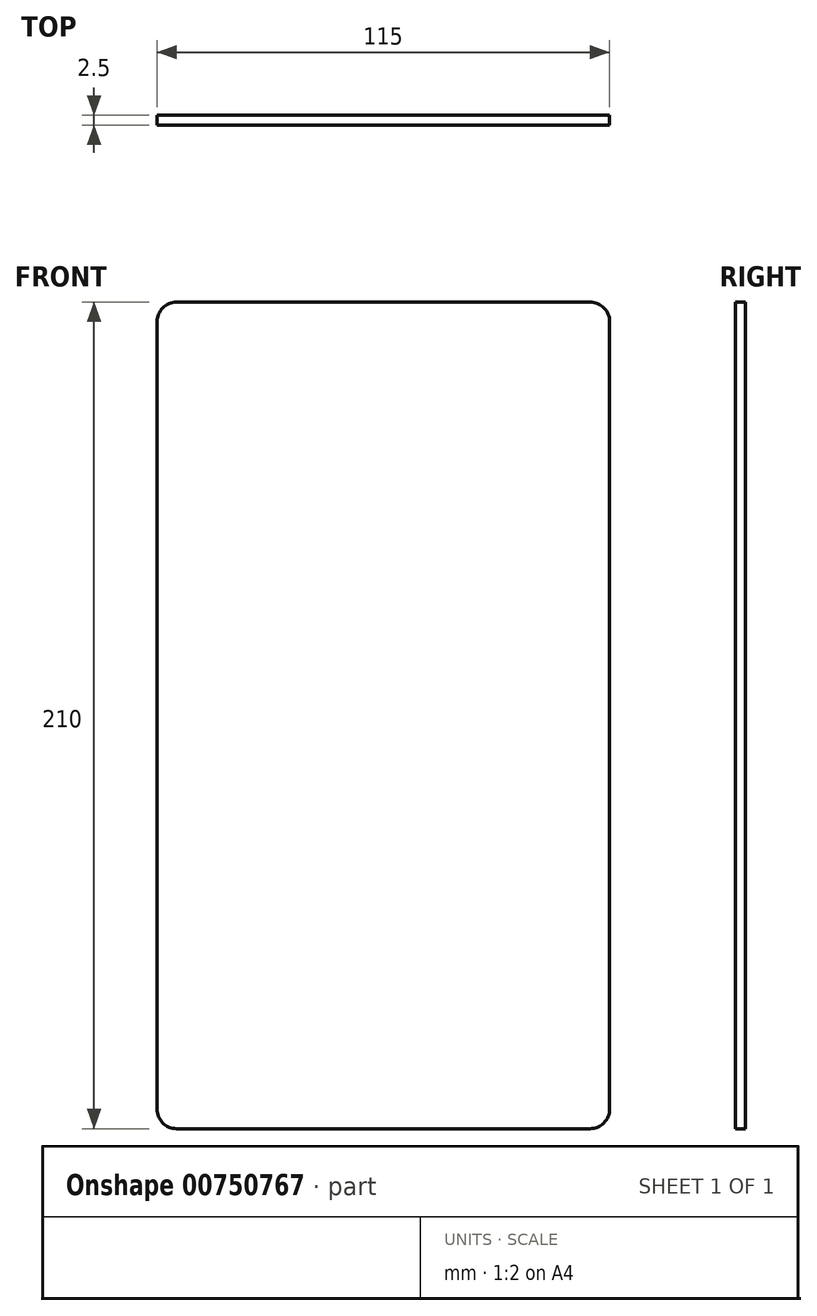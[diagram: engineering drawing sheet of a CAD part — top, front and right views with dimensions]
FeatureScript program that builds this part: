
annotation { "Feature Type Name" : "Feature", "Feature Type Description" : "" }
export const myFeature = defineFeature(function(context is Context, id is Id, definition is map)
    precondition{}
    {
        {
            var Q0;
            Q0=qCreatedBy(makeId("Front.planeOp"),FACE);
            var sketch = newSketch(context, id + "F0", { "sketchPlane" : qUnion([Q0])});
            skLineSegment(sketch, "E0.bottom", {"start": v(5, 0) * mm, "end": v(110, 0) * mm});
            skLineSegment(sketch, "E0.top", {"start": v(5, 210) * mm, "end": v(110, 210) * mm});
            skLineSegment(sketch, "E0.left", {"start": v(0, 5) * mm, "end": v(0, 205) * mm});
            skLineSegment(sketch, "E0.right", {"start": v(115, 5) * mm, "end": v(115, 205) * mm});
            skPoint(sketch, "E1.visualSharp", {"position": v(0, 210) * mm});
            skArc(sketch, "E1.filletArc", {"start": v(5, 210) * mm, "mid": v(1.46, 208.54) * mm, "end": v(0, 205) * mm});
            skPoint(sketch, "E2.visualSharp", {"position": v(115, 210) * mm});
            skArc(sketch, "E2.filletArc", {"start": v(115, 205) * mm, "mid": v(113.54, 208.54) * mm, "end": v(110, 210) * mm});
            skPoint(sketch, "E3.visualSharp", {"position": v(115, 0) * mm});
            skArc(sketch, "E3.filletArc", {"start": v(110, 0) * mm, "mid": v(113.54, 1.46) * mm, "end": v(115, 5) * mm});
            skPoint(sketch, "E4.visualSharp", {"position": v(0, 0) * mm});
            skArc(sketch, "E4.filletArc", {"start": v(0, 5) * mm, "mid": v(1.46, 1.46) * mm, "end": v(5, 0) * mm});
            skSolve(sketch);
        }
        {
            var Q0;
            Q0=makeQuery(id+"F0.imprint","IMPRINT",FACE,{"disambiguationData":[TD([[makeQuery(id+"F0.imprint","IMPRINT",EDGE,{"derivedFrom":sQuery(id+"F0.wireOp",EDGE,"E0.bottom")}),1.0]])]});
            extrude(context, id + "F1", {"entities" : qUnion([Q0]), "depth" : 2.5 * mm, "offsetDistance" : 25 * mm});
        }
    });
